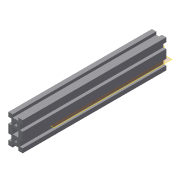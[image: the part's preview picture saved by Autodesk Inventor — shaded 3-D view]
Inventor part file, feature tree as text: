
AUTODESK INVENTOR PART (.ipt)
format: ipt  version: 2019.4 (Build 234330000, 330)  size: 158,720 bytes
history: native  units: mm
features: plane x3, extrude x2, sketch x2, mirror x1, projected_geometry x1
ambient origin geometry x8: Origin, YZ Plane, XZ Plane, XY Plane, X Axis, Y Axis, Z Axis, Center Point
bodies: Solid1 (feature_tree)
feature tree (9):
  extrude  "Extrusion1"  Depth=20.0mm
  plane  "Work Plane1"
  plane  "Work Plane2"
  mirror  "Mirror1"
  extrude  "Extrusion2"  Depth=8.0mm
  plane  "Work Plane3"
  sketch  "Sketch1"  dims[d0=20.0mm d1=20.0mm]
  sketch  "Sketch2"  dims[d2=8.0mm d3=8.0mm d4=8.0mm d5=8.0mm d6=8.0mm d7=8.0mm d8=8.0mm d9=8.0mm d10=200.0mm d11=0.0mm d12=5.0mm d13=4.0mm d14=20.0mm d15=10.0mm d16=10.0mm d17=0.0mm]
  projected_geometry  "Projected Loop1"
